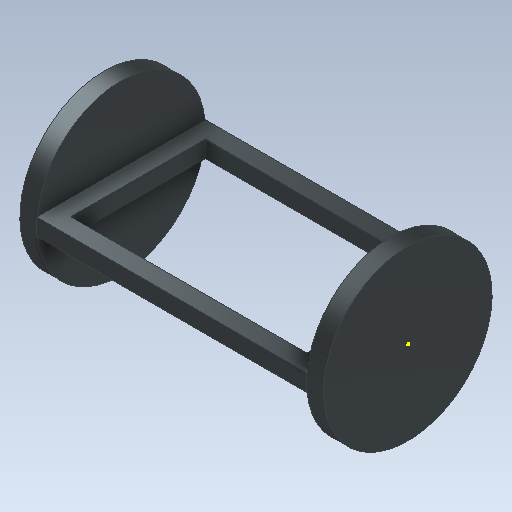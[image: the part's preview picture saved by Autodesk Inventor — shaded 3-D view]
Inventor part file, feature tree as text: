
AUTODESK INVENTOR PART (.ipt)
format: ipt  version: 2020.3 (Build 243373000, 373)  size: 142,336 bytes
history: native  units: mm
features: sketch x3, extrude x2, revolve x1
ambient origin geometry x8: Origin, YZ Plane, XZ Plane, XY Plane, X Axis, Y Axis, Z Axis, Center Point
bodies: Solid1 (feature_tree)
feature tree (6):
  sketch  "Sketch1"  dims[d0=25.0mm d1=5.0mm]
  sketch  "Sketch2"  dims[d2=22.5mm d3=80.0mm]
  revolve  "Revolution1"  [1 undecoded]
  extrude  "Extrusion1"  Depth=80.0mm
  extrude  "Extrusion2"  TaperAngle=90.0deg  [1 undecoded]
  sketch  "Sketch3"  dims[d4=5.0mm d5=90.0deg d6=5.0mm d7=50.0mm d8=0.0mm d9=5.0mm d10=20.0mm d11=0.0mm]
note: 2 required parameter values undecoded (feature->parameter linkage not recoverable at this tier; creation-order binding heuristic only, values carry confidence <= 0.55)